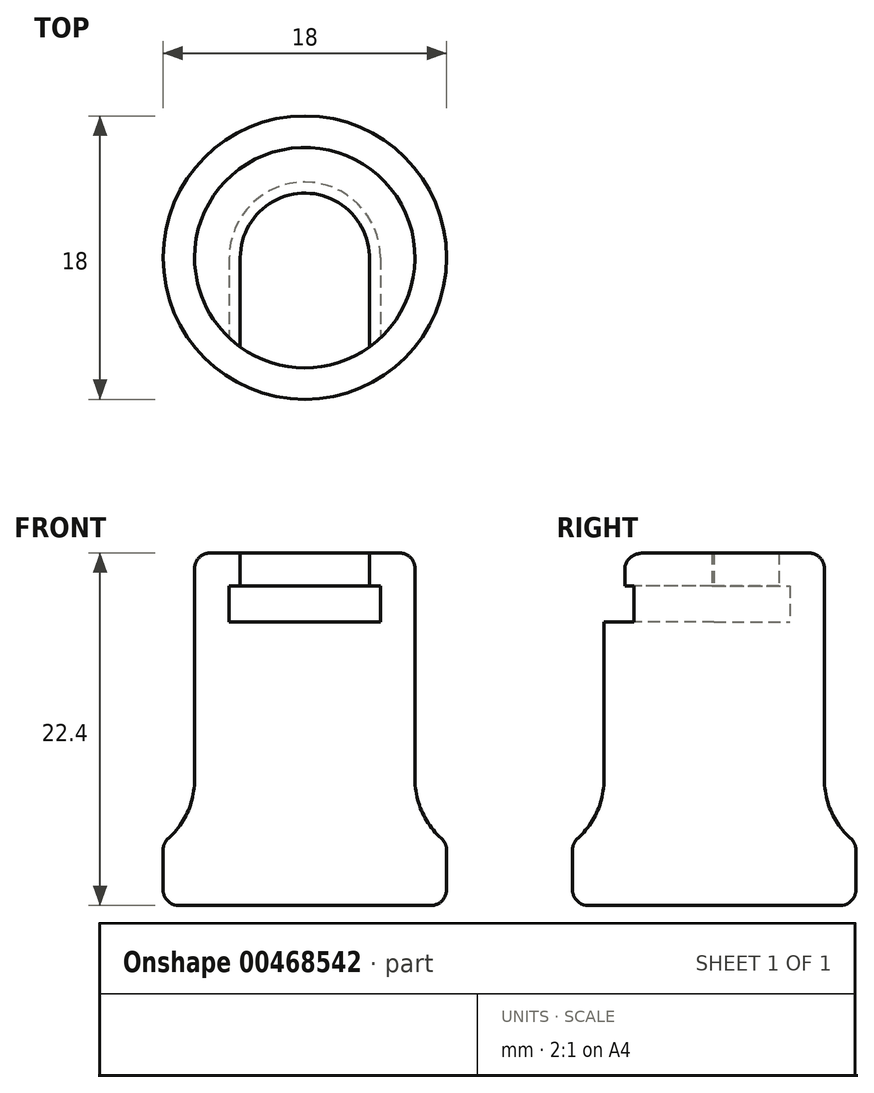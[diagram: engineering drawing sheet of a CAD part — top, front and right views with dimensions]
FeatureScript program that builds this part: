
annotation { "Feature Type Name" : "Feature", "Feature Type Description" : "" }
export const myFeature = defineFeature(function(context is Context, id is Id, definition is map)
    precondition{}
    {
        {
            var Q0;
            Q0=qCreatedBy(makeId("Top.planeOp"),FACE);
            var sketch = newSketch(context, id + "F0", { "sketchPlane" : qUnion([Q0])});
            skCircle(sketch, "E0", {"center": v(0, 0) * mm, "radius": 7 * mm});
            skSolve(sketch);
        }
        {
            var Q0;
            Q0=makeQuery(id+"F0.imprint","IMPRINT",FACE,{"disambiguationData":[TD([[makeQuery(id+"F0.imprint","IMPRINT",EDGE,{"derivedFrom":sQuery(id+"F0.wireOp",EDGE,"E0")}),1.0]])]});
            extrude(context, id + "F1", {"entities" : qUnion([Q0]), "depth" : 18 * mm, "offsetDistance" : 25 * mm});
        }
        {
            var Q0;
            Q0=makeQuery(id+"F1.opExtrude","CAP_FACE",FACE,{"disambiguationData":[OSD([sQuery(id+"F0.wireOp",EDGE,"E0")])],"isStart":false});
            var sketch = newSketch(context, id + "F2", { "sketchPlane" : qUnion([Q0])});
            skCircle(sketch, "E1", {"center": v(0, 0) * mm, "radius": 7 * mm});
            skCircle(sketch, "E2", {"center": v(0, 0) * mm, "radius": 4.8 * mm});
            skSolve(sketch);
        }
        {
            var Q0;
            Q0=makeQuery(id+"F2.imprint","IMPRINT",FACE,{"disambiguationData":[TD([[makeQuery(id+"F2.imprint","IMPRINT",EDGE,{"derivedFrom":sQuery(id+"F2.wireOp",EDGE,"E1")}),1.0]])]});
            extrude(context, id + "F3", {"entities" : qUnion([Q0]), "operationType" : NewBodyOperationType.ADD, "depth" : 2.3 * mm, "offsetDistance" : 25 * mm});
        }
        {
            var Q0;
            Q0=makeQuery(id+"F3.opExtrude","CAP_FACE",FACE,{"disambiguationData":[OSD([sQuery(id+"F2.wireOp",EDGE,"E1"),sQuery(id+"F2.wireOp",EDGE,"E2")])],"isStart":false});
            cPlane(context, id + "F4", {"entities" : qUnion([Q0]), "cplaneType" : CPlaneType.OFFSET, "offset" : 0 * mm, "width" : 150 * mm, "height" : 150 * mm});
        }
        {
            var Q0;
            Q0=qCreatedBy(id+"F4.planeOp",FACE);
            var sketch = newSketch(context, id + "F5", { "sketchPlane" : qUnion([Q0])});
            skCircle(sketch, "E3", {"center": v(0, 0) * mm, "radius": 7 * mm});
            skCircle(sketch, "E4", {"center": v(0, 0) * mm, "radius": 4.1 * mm});
            skLineSegment(sketch, "E5.bottom", {"start": v(-4.8, 0) * mm, "end": v(4.8, 0) * mm});
            skLineSegment(sketch, "E5.top", {"start": v(-4.8, -7.19) * mm, "end": v(4.8, -7.19) * mm});
            skLineSegment(sketch, "E5.left", {"start": v(-4.8, 0) * mm, "end": v(-4.8, -7.19) * mm});
            skLineSegment(sketch, "E5.right", {"start": v(4.8, 0) * mm, "end": v(4.8, -7.19) * mm});
            skSolve(sketch);
        }
        {
            var Q0;
            Q0=makeQuery(id+"F5.imprint","IMPRINT",FACE,{"disambiguationData":[TD([[makeQuery(id+"F5.imprint","IMPRINT",EDGE,{"derivedFrom":sQuery(id+"F5.wireOp",EDGE,"E3")}),1.0]])]});
            extrude(context, id + "F6", {"entities" : qUnion([Q0]), "operationType" : NewBodyOperationType.ADD, "depth" : 2.1 * mm, "offsetDistance" : 25 * mm});
        }
        {
            var Q0;
            Q0=makeQuery(id+"F6.opExtrude","CAP_FACE",FACE,{"disambiguationData":[OSD([sQuery(id+"F5.wireOp",EDGE,"E3"),sQuery(id+"F5.wireOp",EDGE,"E4")])],"isStart":false});
            cPlane(context, id + "F7", {"entities" : qUnion([Q0]), "cplaneType" : CPlaneType.OFFSET, "offset" : 0 * mm, "width" : 150 * mm, "height" : 150 * mm});
        }
        {
            var Q0;
            Q0=qCreatedBy(id+"F7.planeOp",FACE);
            var sketch = newSketch(context, id + "F8", { "sketchPlane" : qUnion([Q0])});
            skLineSegment(sketch, "E6.bottom", {"start": v(-4.1, 0) * mm, "end": v(4.1, 0) * mm});
            skLineSegment(sketch, "E6.top", {"start": v(-4.1, -7.39) * mm, "end": v(4.1, -7.39) * mm});
            skLineSegment(sketch, "E6.left", {"start": v(-4.1, 0) * mm, "end": v(-4.1, -7.39) * mm});
            skLineSegment(sketch, "E6.right", {"start": v(4.1, 0) * mm, "end": v(4.1, -7.39) * mm});
            skSolve(sketch);
        }
        {
            var Q0;
            Q0=makeQuery(id+"F8.imprint","IMPRINT",FACE,{"disambiguationData":[TD([[makeQuery(id+"F8.imprint","IMPRINT",EDGE,{"derivedFrom":sQuery(id+"F8.wireOp",EDGE,"E6.bottom")}),-1.0]])]});
            extrude(context, id + "F9", {"entities" : qUnion([Q0]), "operationType" : NewBodyOperationType.REMOVE, "oppositeDirection" : true, "depth" : 4.4 * mm, "offsetDistance" : 25 * mm});
        }
        {
            var Q0;
            {var subQ6=sQuery(id+"F5.wireOp",EDGE,"E5.left");var subQ8=sQuery(id+"F5.wireOp",EDGE,"E3");var subQ9=makeQuery(id+"F5.imprint","INTERSECT",VERTEX,{"derivedFrom":[subQ8,subQ6]});Q0=makeQuery(id+"F5.imprint","IMPRINT",FACE,{"disambiguationData":[TD([[makeQuery(id+"F5.imprint","IMPRINT",EDGE,{"disambiguationData":[TD([[subQ9,-1.0]])],"derivedFrom":subQ8}),1.0]])]});}
            extrude(context, id + "F10", {"entities" : qUnion([Q0]), "operationType" : NewBodyOperationType.REMOVE, "oppositeDirection" : true, "depth" : 2.3 * mm, "offsetDistance" : 25 * mm});
        }
        {
            var Q0;
            Q0=makeQuery(id+"F1.opExtrude","CAP_FACE",FACE,{"disambiguationData":[OSD([sQuery(id+"F0.wireOp",EDGE,"E0")])],"isStart":true});
            var sketch = newSketch(context, id + "F11", { "sketchPlane" : qUnion([Q0])});
            skCircle(sketch, "E7", {"center": v(0, 0) * mm, "radius": 9 * mm});
            skSolve(sketch);
        }
        {
            var Q0;
            Q0=makeQuery(id+"F11.imprint","IMPRINT",FACE,{"disambiguationData":[TD([[makeQuery(id+"F11.imprint","IMPRINT",EDGE,{"derivedFrom":makeQuery(id+"F1.opExtrude","CAP_EDGE",EDGE,{"disambiguationData":[OSD([sQuery(id+"F0.wireOp",EDGE,"E0")])],"isStart":true})}),-1.0]])]});
            var Q1;
            Q1=makeQuery(id+"F11.imprint","IMPRINT",FACE,{"disambiguationData":[TD([[makeQuery(id+"F11.imprint","IMPRINT",EDGE,{"derivedFrom":sQuery(id+"F11.wireOp",EDGE,"E7")}),1.0]])]});
            extrude(context, id + "F12", {"entities" : qUnion([Q0, Q1]), "operationType" : NewBodyOperationType.ADD, "oppositeDirection" : true, "depth" : 4 * mm, "offsetDistance" : 25 * mm});
        }
        {
            var Q0;
            Q0=makeQuery(id+"F12.boolean.opBoolean","INTERSECT",EDGE,{"derivedFrom":[makeQuery(id+"F6.boolean.opBoolean","MERGE",FACE,{"derivedFrom":[makeQuery(id+"F3.boolean.opBoolean","MERGE",FACE,{"derivedFrom":[makeQuery(id+"F1.opExtrude","SWEPT_FACE",FACE,{"disambiguationData":[OSD([sQuery(id+"F0.wireOp",EDGE,"E0")])]}),makeQuery(id+"F3.opExtrude","SWEPT_FACE",FACE,{"disambiguationData":[OSD([sQuery(id+"F2.wireOp",EDGE,"E1")])]})]}),makeQuery(id+"F6.opExtrude","SWEPT_FACE",FACE,{"disambiguationData":[OSD([sQuery(id+"F5.wireOp",EDGE,"E3")])]})]}),makeQuery(id+"F12.opExtrude","CAP_FACE",FACE,{"disambiguationData":[OSD([sQuery(id+"F11.wireOp",EDGE,"E7")])],"isStart":false})]});
            fillet(context, id + "F13", {"entities" : qUnion([Q0]), "tangentPropagation" : true, "radius" : 5 * mm, "defaultsChanged" : false, "vertexSettings" : [], "allowEdgeOverflow" : false});
        }
        {
            var Q0;
            {var subQ0=sQuery(id+"F11.wireOp",EDGE,"E7");Q0=makeQuery(id+"F13.opFillet","BLEND_EDGE",EDGE,{"blendedFrom":[makeQuery(id+"F12.boolean.opBoolean","INTERSECT",EDGE,{"derivedFrom":[makeQuery(id+"F6.boolean.opBoolean","MERGE",FACE,{"derivedFrom":[makeQuery(id+"F3.boolean.opBoolean","MERGE",FACE,{"derivedFrom":[makeQuery(id+"F1.opExtrude","SWEPT_FACE",FACE,{"disambiguationData":[OSD([sQuery(id+"F0.wireOp",EDGE,"E0")])]}),makeQuery(id+"F3.opExtrude","SWEPT_FACE",FACE,{"disambiguationData":[OSD([sQuery(id+"F2.wireOp",EDGE,"E1")])]})]}),makeQuery(id+"F6.opExtrude","SWEPT_FACE",FACE,{"disambiguationData":[OSD([sQuery(id+"F5.wireOp",EDGE,"E3")])]})]}),makeQuery(id+"F12.opExtrude","CAP_FACE",FACE,{"disambiguationData":[OSD([subQ0])],"isStart":false})]}),makeQuery(id+"F12.opExtrude","SWEPT_FACE",FACE,{"disambiguationData":[OSD([subQ0])]})],"blendedInto":[makeQuery(id+"F12.opExtrude","SWEPT_FACE",FACE,{"disambiguationData":[OSD([subQ0])]})]});}
            fillet(context, id + "F14", {"entities" : qUnion([Q0]), "tangentPropagation" : true, "radius" : 1 * mm, "defaultsChanged" : true, "vertexSettings" : [], "allowEdgeOverflow" : false});
        }
        {
            var Q0;
            Q0=makeQuery(id+"F12.opExtrude","CAP_EDGE",EDGE,{"disambiguationData":[OSD([sQuery(id+"F11.wireOp",EDGE,"E7")])],"isStart":true});
            fillet(context, id + "F15", {"entities" : qUnion([Q0]), "tangentPropagation" : true, "radius" : 1 * mm, "defaultsChanged" : true, "vertexSettings" : [], "allowEdgeOverflow" : false});
        }
        {
            var Q0;
            Q0=makeQuery(id+"F6.opExtrude","CAP_EDGE",EDGE,{"disambiguationData":[OSD([sQuery(id+"F5.wireOp",EDGE,"E3")])],"isStart":false});
            fillet(context, id + "F16", {"entities" : qUnion([Q0]), "tangentPropagation" : true, "radius" : 1 * mm, "defaultsChanged" : true, "vertexSettings" : [], "allowEdgeOverflow" : false});
        }
    });
